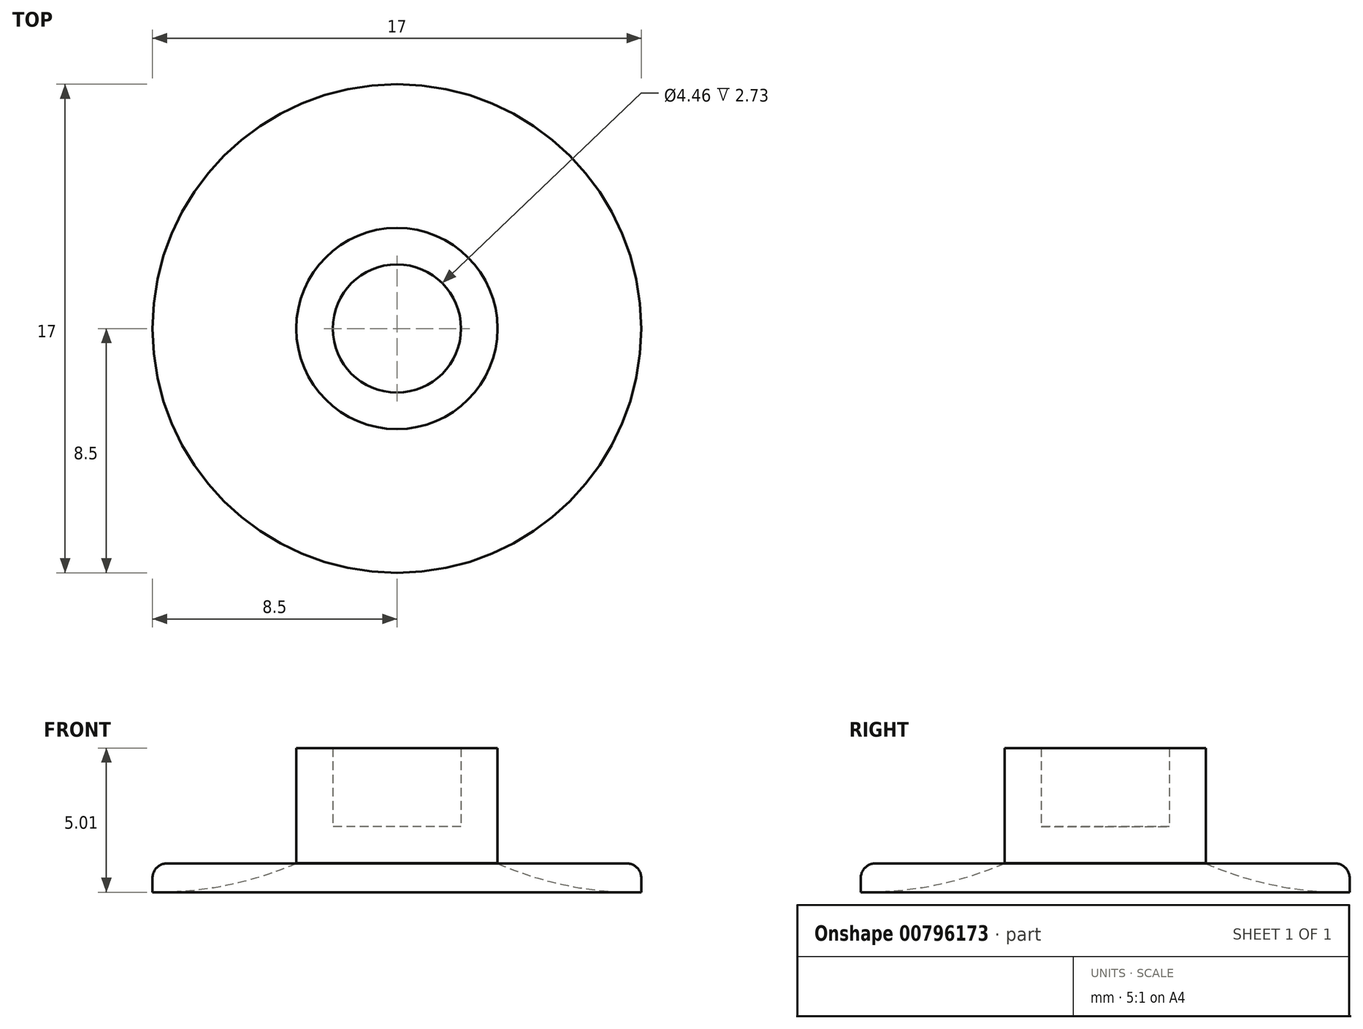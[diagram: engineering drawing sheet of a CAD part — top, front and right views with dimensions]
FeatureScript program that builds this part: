
annotation { "Feature Type Name" : "Feature", "Feature Type Description" : "" }
export const myFeature = defineFeature(function(context is Context, id is Id, definition is map)
    precondition{}
    {
        {
            var Q0;
            Q0=qCreatedBy(makeId("Top.planeOp"),FACE);
            var sketch = newSketch(context, id + "F0", { "sketchPlane" : qUnion([Q0])});
            skCircle(sketch, "E0", {"center": v(0, 0) * mm, "radius": 3.5 * mm});
            skCircle(sketch, "E1", {"center": v(0, 0) * mm, "radius": 8.5 * mm});
            skSolve(sketch);
        }
        {
            var Q0;
            Q0=makeQuery(id+"F0.imprint","IMPRINT",FACE,{"disambiguationData":[TD([[makeQuery(id+"F0.imprint","IMPRINT",EDGE,{"derivedFrom":sQuery(id+"F0.wireOp",EDGE,"E0")}),1.0]])]});
            extrude(context, id + "F1", {"entities" : qUnion([Q0]), "depth" : 4 * mm, "offsetDistance" : 25.4 * mm});
        }
        {
            var Q0;
            Q0=makeQuery(id+"F0.imprint","IMPRINT",FACE,{"disambiguationData":[TD([[makeQuery(id+"F0.imprint","IMPRINT",EDGE,{"derivedFrom":sQuery(id+"F0.wireOp",EDGE,"E0")}),-1.0]])]});
            extrude(context, id + "F2", {"entities" : qUnion([Q0]), "depth" : 1 * mm, "offsetDistance" : 25.4 * mm});
        }
        {
            var Q0;
            Q0=makeQuery(id+"F2.opExtrude","CAP_EDGE",EDGE,{"disambiguationData":[OSD([sQuery(id+"F0.wireOp",EDGE,"E1")])],"isStart":false});
            fillet(context, id + "F3", {"entities" : qUnion([Q0]), "radius" : 0.5 * mm, "tangentPropagation" : true, "allowEdgeOverflow" : false});
        }
        {
            var Q0;
            Q0=makeQuery(id+"F1.opExtrude","CAP_FACE",FACE,{"disambiguationData":[OSD([sQuery(id+"F0.wireOp",EDGE,"E0")])],"isStart":false});
            shell(context, id + "F4", {"entities" : qUnion([Q0]), "thickness" : 1.27 * mm});
        }
        {
            var Q0;
            Q0=makeQuery(id+"F2.opExtrude","SWEPT_BODY",BODY,{"disambiguationData":[OSD([sQuery(id+"F0.wireOp",EDGE,"E0"),sQuery(id+"F0.wireOp",EDGE,"E1")])]});
            transform(context, id + "F5", {"entities" : qUnion([Q0]), "transformType" : TransformType.TRANSLATION_3D, "dx" : 0 * mm, "dy" : 0 * mm, "dz" : -1.01 * mm, "makeCopy" : false});
        }
        {
            var Q0;
            Q0=makeQuery(id+"F2.opExtrude","CAP_EDGE",EDGE,{"disambiguationData":[OSD([sQuery(id+"F0.wireOp",EDGE,"E0")])],"isStart":true});
            fillet(context, id + "F6", {"entities" : qUnion([Q0]), "radius" : 11.9 * mm, "tangentPropagation" : true, "allowEdgeOverflow" : false});
        }
    });
